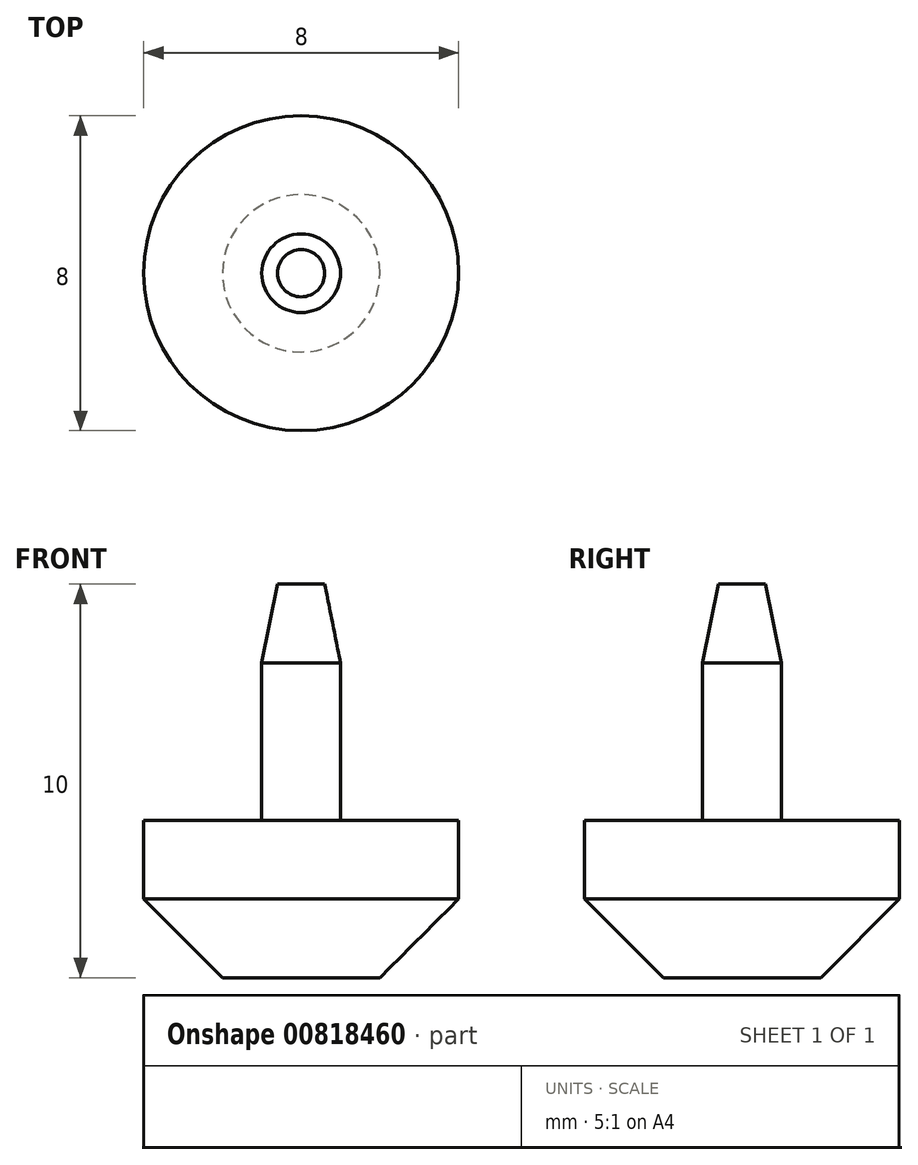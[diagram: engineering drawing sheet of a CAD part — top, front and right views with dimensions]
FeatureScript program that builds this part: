
annotation { "Feature Type Name" : "Feature", "Feature Type Description" : "" }
export const myFeature = defineFeature(function(context is Context, id is Id, definition is map)
    precondition{}
    {
        {
            var Q0;
            Q0=qCreatedBy(makeId("Top.planeOp"),FACE);
            var sketch = newSketch(context, id + "F0", { "sketchPlane" : qUnion([Q0])});
            skCircle(sketch, "E0", {"center": v(0, 0) * mm, "radius": 4 * mm});
            skSolve(sketch);
        }
        {
            var Q0;
            Q0=makeQuery(id+"F0.imprint","IMPRINT",FACE,{"disambiguationData":[TD([[makeQuery(id+"F0.imprint","IMPRINT",EDGE,{"derivedFrom":sQuery(id+"F0.wireOp",EDGE,"E0")}),1.0]])]});
            extrude(context, id + "F1", {"entities" : qUnion([Q0]), "depth" : 4 * mm, "offsetDistance" : 25 * mm});
        }
        {
            var Q0;
            Q0=makeQuery(id+"F1.opExtrude","CAP_FACE",FACE,{"disambiguationData":[OSD([sQuery(id+"F0.wireOp",EDGE,"E0")])],"isStart":false});
            var sketch = newSketch(context, id + "F2", { "sketchPlane" : qUnion([Q0])});
            skCircle(sketch, "E1", {"center": v(0, 0) * mm, "radius": 1 * mm});
            skSolve(sketch);
        }
        {
            var Q0;
            Q0 = qSketchRegion(id + "F2", true);
            extrude(context, id + "F3", {"entities" : qUnion([Q0]), "operationType" : NewBodyOperationType.ADD, "depth" : 6 * mm, "offsetDistance" : 25 * mm});
        }
        {
            var Q0;
            Q0=makeQuery(id+"F3.opExtrude","CAP_EDGE",EDGE,{"disambiguationData":[OSD([sQuery(id+"F2.wireOp",EDGE,"E1")])],"isStart":false});
            chamfer(context, id + "F4", {"entities" : qUnion([Q0]), "chamferType" : ChamferType.TWO_OFFSETS, "width1" : .4 * mm, "oppositeDirection" : false, "width2" : 2 * mm, "tangentPropagation" : true});
        }
        {
            var Q0;
            Q0=makeQuery(id+"F1.opExtrude","CAP_EDGE",EDGE,{"disambiguationData":[OSD([sQuery(id+"F0.wireOp",EDGE,"E0")])],"isStart":true});
            chamfer(context, id + "F5", {"entities" : qUnion([Q0]), "chamferType" : ChamferType.OFFSET_ANGLE, "width" : 2 * mm, "oppositeDirection" : false, "angle" : 45 * degree, "tangentPropagation" : true});
        }
    });
